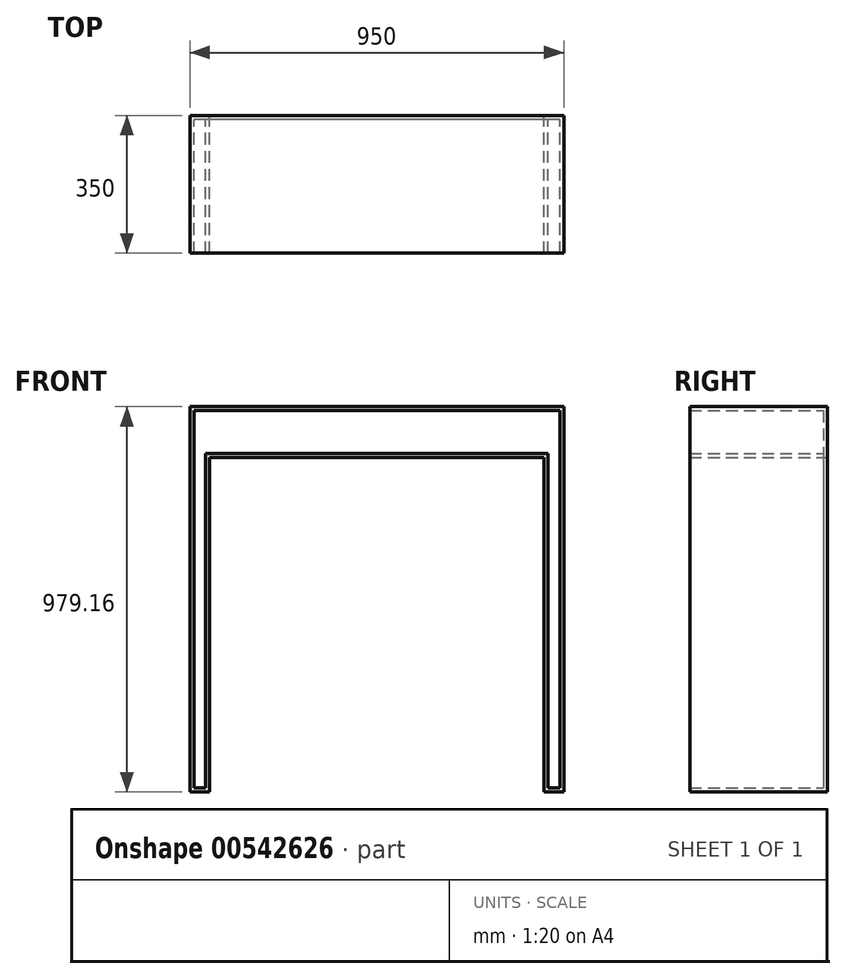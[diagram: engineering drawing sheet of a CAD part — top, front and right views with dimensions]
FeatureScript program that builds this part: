
annotation { "Feature Type Name" : "Feature", "Feature Type Description" : "" }
export const myFeature = defineFeature(function(context is Context, id is Id, definition is map)
    precondition{}
    {
        {
            var Q0;
            Q0=qCreatedBy(makeId("Top.planeOp"),FACE);
            var sketch = newSketch(context, id + "F0", { "sketchPlane" : qUnion([Q0])});
            skLineSegment(sketch, "E0.bottom", {"start": v(475, -175) * mm, "end": v(-475, -175) * mm});
            skLineSegment(sketch, "E0.top", {"start": v(475, 175) * mm, "end": v(-475, 175) * mm});
            skLineSegment(sketch, "E0.left", {"start": v(475, -175) * mm, "end": v(475, 175) * mm});
            skLineSegment(sketch, "E0.right", {"start": v(-475, -175) * mm, "end": v(-475, 175) * mm});
            skPoint(sketch, "E0.middle", {"position": v(0, 0) * mm});
            skSolve(sketch);
        }
        {
            var Q0;
            Q0 = qSketchRegion(id + "F0", true);
            extrude(context, id + "F1", {"entities" : qUnion([Q0]), "depth" : 900 * mm, "offsetDistance" : 25 * mm});
        }
        {
            var Q0;
            Q0=makeQuery(id+"F1.opExtrude","SWEPT_FACE",FACE,{"disambiguationData":[OSD([sQuery(id+"F0.wireOp",EDGE,"E0.bottom")])]});
            var Q1;
            Q1=makeQuery(id+"F1.opExtrude","CAP_FACE",FACE,{"disambiguationData":[OSD([sQuery(id+"F0.wireOp",EDGE,"E0.bottom"),sQuery(id+"F0.wireOp",EDGE,"E0.top"),sQuery(id+"F0.wireOp",EDGE,"E0.left"),sQuery(id+"F0.wireOp",EDGE,"E0.right")])],"isStart":true});
            var Q2;
            Q2=makeQuery(id+"F1.opExtrude","SWEPT_FACE",FACE,{"disambiguationData":[OSD([sQuery(id+"F0.wireOp",EDGE,"E0.top")])]});
            shell(context, id + "F2", {"entities" : qUnion([Q0, Q1, Q2]), "thickness" : 50 * mm});
        }
        {
            var Q0;
            Q0=makeQuery(id+"F1.opExtrude","CAP_FACE",FACE,{"disambiguationData":[OSD([sQuery(id+"F0.wireOp",EDGE,"E0.bottom"),sQuery(id+"F0.wireOp",EDGE,"E0.top"),sQuery(id+"F0.wireOp",EDGE,"E0.left"),sQuery(id+"F0.wireOp",EDGE,"E0.right")])],"isStart":false});
            var sketch = newSketch(context, id + "F3", { "sketchPlane" : qUnion([Q0])});
            skSolve(sketch);
        }
        {
            var Q0;
            Q0=makeQuery(id+"F3.imprint","IMPRINT",FACE,{"disambiguationData":[TD([[makeQuery(id+"F3.imprint","IMPRINT",EDGE,{"derivedFrom":makeQuery(id+"F1.opExtrude","CAP_EDGE",EDGE,{"disambiguationData":[OSD([sQuery(id+"F0.wireOp",EDGE,"E0.bottom")])],"isStart":false})}),-1.0]])]});
            extrude(context, id + "F4", {"entities" : qUnion([Q0]), "operationType" : NewBodyOperationType.ADD, "depth" : 79.16 * mm, "offsetDistance" : 25 * mm});
        }
        {
            var Q0;
            {var subQ0=sQuery(id+"F0.wireOp",EDGE,"E0.bottom");Q0=makeQuery(id+"F4.boolean.opBoolean","MERGE",FACE,{"derivedFrom":[makeQuery(id+"F1.opExtrude","SWEPT_FACE",FACE,{"disambiguationData":[OSD([subQ0])]}),makeQuery(id+"F4.opExtrude","SWEPT_FACE",FACE,{"disambiguationData":[OSD([subQ0])]})]});}
            shell(context, id + "F5", {"entities" : qUnion([Q0]), "thickness" : 10 * mm});
        }
    });
